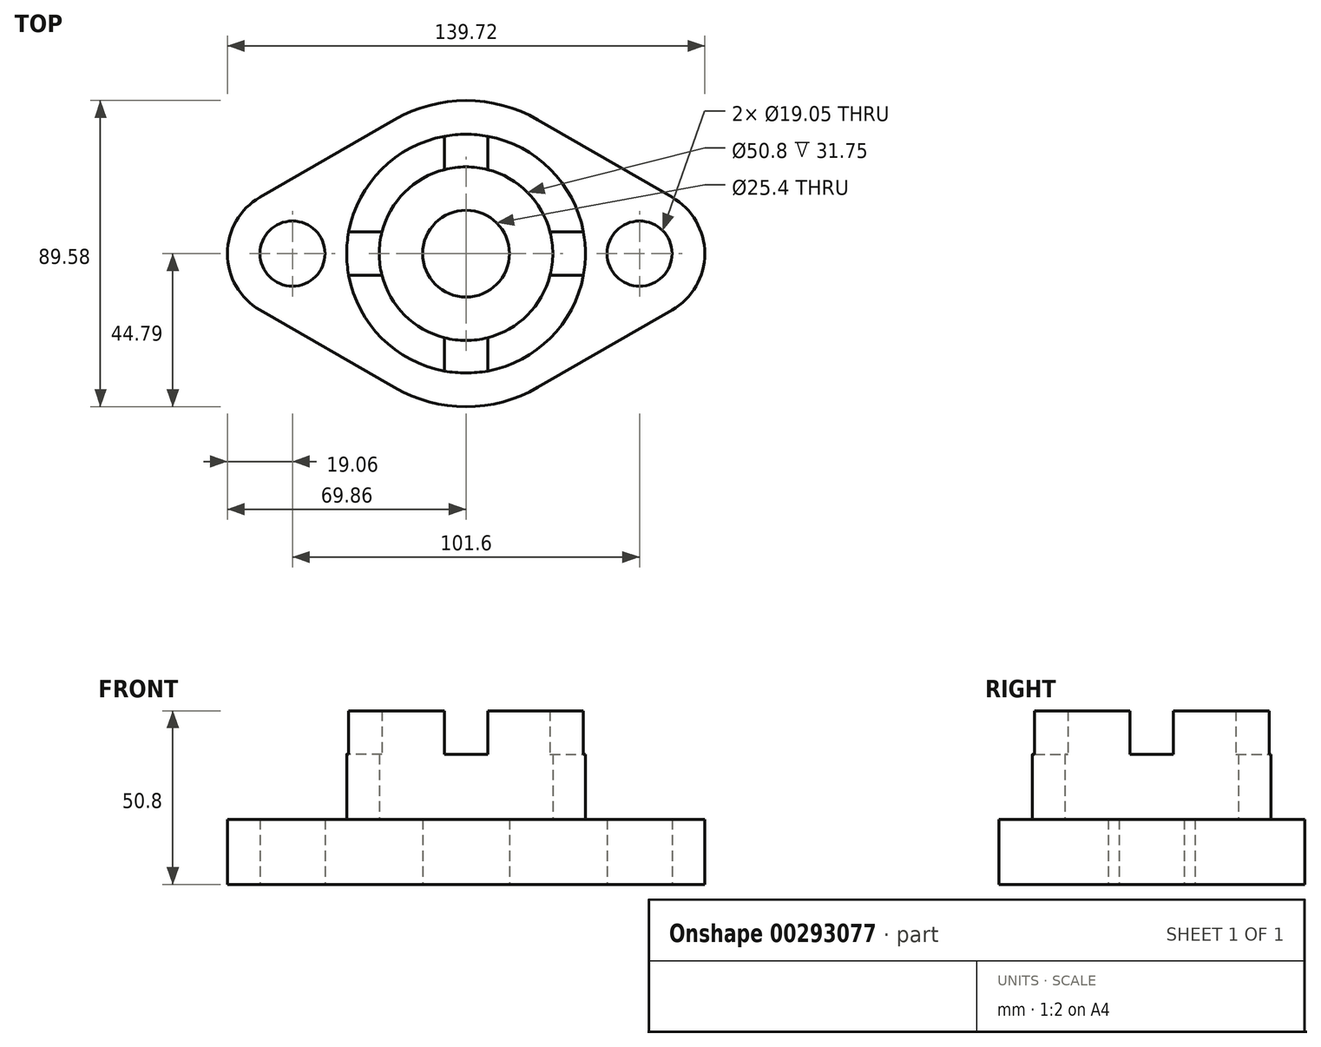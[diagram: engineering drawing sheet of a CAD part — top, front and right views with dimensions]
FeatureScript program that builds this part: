
annotation { "Feature Type Name" : "Feature", "Feature Type Description" : "" }
export const myFeature = defineFeature(function(context is Context, id is Id, definition is map)
    precondition{}
    {
        {
            var Q0;
            Q0=qCreatedBy(makeId("Top.planeOp"),FACE);
            var sketch = newSketch(context, id + "F0", { "sketchPlane" : qUnion([Q0])});
            skCircle(sketch, "E0", {"center": v(0, 0) * mm, "radius": 12.7 * mm});
            skCircle(sketch, "E1", {"center": v(0, 0) * mm, "radius": 25.4 * mm});
            skCircle(sketch, "E2", {"center": v(0, 0) * mm, "radius": 34.93 * mm});
            skCircle(sketch, "E3", {"center": v(-50.8, 0) * mm, "radius": 9.53 * mm});
            skCircle(sketch, "E4", {"center": v(50.8, 0) * mm, "radius": 9.53 * mm});
            skLineSegment(sketch, "E5", {"start": v(-21.04, -39.16) * mm, "end": v(-60.32, -16.5) * mm});
            skLineSegment(sketch, "E6", {"start": v(-60.33, 16.5) * mm, "end": v(-21.04, 39.16) * mm});
            skLineSegment(sketch, "E7", {"start": v(21.04, -39.16) * mm, "end": v(60.32, -16.5) * mm});
            skLineSegment(sketch, "E8", {"start": v(60.33, 16.5) * mm, "end": v(21.04, 39.16) * mm});
            skArc(sketch, "E9", {"start": v(-60.33, 16.5) * mm, "mid": v(-69.86, 0) * mm, "end": v(-60.32, -16.5) * mm});
            skArc(sketch, "E10", {"start": v(60.32, -16.5) * mm, "mid": v(69.86, 0) * mm, "end": v(60.33, 16.5) * mm});
            skArc(sketch, "E11", {"start": v(21.04, 39.16) * mm, "mid": v(0, 44.79) * mm, "end": v(-21.04, 39.16) * mm});
            skArc(sketch, "E12", {"start": v(-21.04, -39.16) * mm, "mid": v(0, -44.79) * mm, "end": v(21.04, -39.16) * mm});
            skLineSegment(sketch, "E13", {"start": v(-6.35, -34.34) * mm, "end": v(-6.35, -24.6) * mm});
            skLineSegment(sketch, "E14", {"start": v(6.35, -24.6) * mm, "end": v(6.35, -34.34) * mm});
            skLineSegment(sketch, "E15", {"start": v(34.34, -6.35) * mm, "end": v(24.6, -6.35) * mm});
            skLineSegment(sketch, "E16", {"start": v(24.6, 6.35) * mm, "end": v(34.34, 6.35) * mm});
            skLineSegment(sketch, "E17", {"start": v(-6.35, 34.34) * mm, "end": v(-6.35, 24.6) * mm});
            skLineSegment(sketch, "E18", {"start": v(6.35, 24.6) * mm, "end": v(6.35, 34.34) * mm});
            skLineSegment(sketch, "E19", {"start": v(-34.34, -6.35) * mm, "end": v(-24.6, -6.35) * mm});
            skLineSegment(sketch, "E20", {"start": v(-24.6, 6.35) * mm, "end": v(-34.34, 6.35) * mm});
            skSolve(sketch);
        }
        {
            var Q0;
            Q0=makeQuery(id+"F0.imprint","IMPRINT",FACE,{"disambiguationData":[TD([[makeQuery(id+"F0.imprint","IMPRINT",EDGE,{"derivedFrom":sQuery(id+"F0.wireOp",EDGE,"E1")}),-1.0]])]});
            extrude(context, id + "F1", {"entities" : qUnion([Q0]), "depth" : 38.1 * mm});
        }
        {
            var Q0;
            Q0 = qSketchRegion(id + "F0", true);
            extrude(context, id + "F2", {"entities" : qUnion([Q0]), "operationType" : NewBodyOperationType.ADD, "depth" : 19.05 * mm});
        }
        {
            var Q0;
            Q0=makeQuery(id+"F0.imprint","IMPRINT",FACE,{"disambiguationData":[TD([[makeQuery(id+"F0.imprint","IMPRINT",EDGE,{"derivedFrom":sQuery(id+"F0.wireOp",EDGE,"E0")}),-1.0]])]});
            extrude(context, id + "F3", {"entities" : qUnion([Q0]), "operationType" : NewBodyOperationType.ADD, "depth" : 19.05 * mm});
        }
        {
            var Q0;
            {var subQ0=sQuery(id+"F0.wireOp",EDGE,"E17");Q0=makeQuery(id+"F0.imprint","IMPRINT",FACE,{"disambiguationData":[TD([[makeQuery(id+"F0.imprint","IMPRINT",EDGE,{"derivedFrom":subQ0}),-1.0]])]});}
            var Q1;
            {var subQ0=sQuery(id+"F0.wireOp",EDGE,"E16");Q1=makeQuery(id+"F0.imprint","IMPRINT",FACE,{"disambiguationData":[TD([[makeQuery(id+"F0.imprint","IMPRINT",EDGE,{"derivedFrom":subQ0}),1.0]])]});}
            var Q2;
            {var subQ0=sQuery(id+"F0.wireOp",EDGE,"E14");Q2=makeQuery(id+"F0.imprint","IMPRINT",FACE,{"disambiguationData":[TD([[makeQuery(id+"F0.imprint","IMPRINT",EDGE,{"derivedFrom":subQ0}),1.0]])]});}
            var Q3;
            {var subQ0=sQuery(id+"F0.wireOp",EDGE,"E13");Q3=makeQuery(id+"F0.imprint","IMPRINT",FACE,{"disambiguationData":[TD([[makeQuery(id+"F0.imprint","IMPRINT",EDGE,{"derivedFrom":subQ0}),1.0]])]});}
            extrude(context, id + "F4", {"entities" : qUnion([Q0, Q1, Q2, Q3]), "operationType" : NewBodyOperationType.ADD, "depth" : 50.8 * mm});
        }
    });
